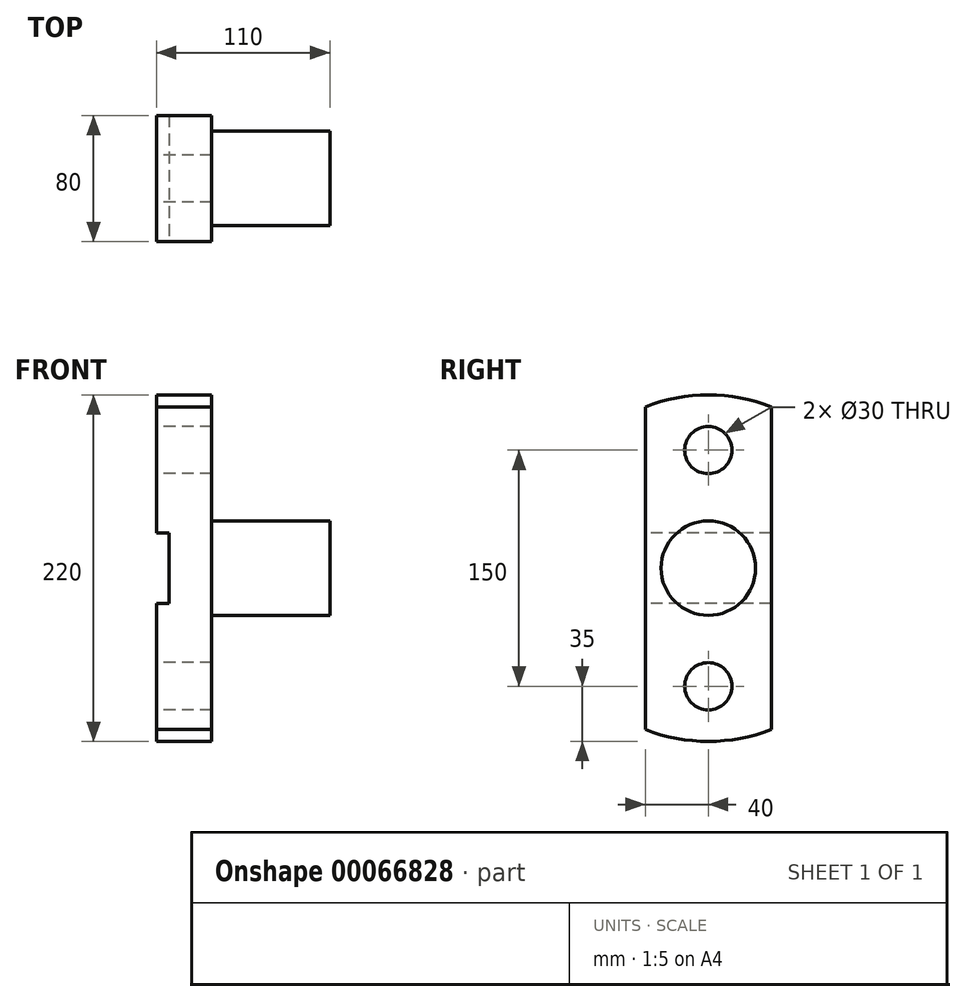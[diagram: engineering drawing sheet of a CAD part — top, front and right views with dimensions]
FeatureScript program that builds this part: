
annotation { "Feature Type Name" : "Feature", "Feature Type Description" : "" }
export const myFeature = defineFeature(function(context is Context, id is Id, definition is map)
    precondition{}
    {
        {
            var Q0;
            Q0=qCreatedBy(makeId("Right.planeOp"),FACE);
            var sketch = newSketch(context, id + "F0", { "sketchPlane" : qUnion([Q0])});
            skArc(sketch, "E0", {"start": v(-40, -102.47) * mm, "mid": v(0, -110) * mm, "end": v(40, -102.47) * mm});
            skLineSegment(sketch, "E1", {"start": v(-40, 102.47) * mm, "end": v(-40, -102.47) * mm});
            skLineSegment(sketch, "E2", {"start": v(40, 102.47) * mm, "end": v(40, -102.47) * mm});
            skArc(sketch, "E3.trimOffspring", {"start": v(40, 102.47) * mm, "mid": v(0, 110) * mm, "end": v(-40, 102.47) * mm});
            skCircle(sketch, "E4", {"center": v(0, 75) * mm, "radius": 15 * mm});
            skCircle(sketch, "E5", {"center": v(0, -75) * mm, "radius": 15 * mm});
            skSolve(sketch);
        }
        {
            var Q0;
            Q0=makeQuery(id+"F0.imprint","IMPRINT",FACE,{"disambiguationData":[TD([[makeQuery(id+"F0.imprint","IMPRINT",EDGE,{"derivedFrom":sQuery(id+"F0.wireOp",EDGE,"E0")}),1.0]])]});
            extrude(context, id + "F1", {"entities" : qUnion([Q0]), "depth" : 35 * mm});
        }
        {
            var Q0;
            Q0=makeQuery(id+"F1.opExtrude","CAP_FACE",FACE,{"disambiguationData":[OSD([sQuery(id+"F0.wireOp",EDGE,"E0"),sQuery(id+"F0.wireOp",EDGE,"E1"),sQuery(id+"F0.wireOp",EDGE,"E2"),sQuery(id+"F0.wireOp",EDGE,"E3.trimOffspring"),sQuery(id+"F0.wireOp",EDGE,"E4"),sQuery(id+"F0.wireOp",EDGE,"E5")])],"isStart":false});
            var sketch = newSketch(context, id + "F2", { "sketchPlane" : qUnion([Q0])});
            skCircle(sketch, "E6", {"center": v(0, 0) * mm, "radius": 30 * mm});
            skSolve(sketch);
        }
        {
            var Q0;
            Q0=makeQuery(id+"F2.imprint","IMPRINT",FACE,{"disambiguationData":[TD([[makeQuery(id+"F2.imprint","IMPRINT",EDGE,{"derivedFrom":sQuery(id+"F2.wireOp",EDGE,"E6")}),1.0]])]});
            extrude(context, id + "F3", {"entities" : qUnion([Q0]), "operationType" : NewBodyOperationType.ADD, "depth" : 75 * mm});
        }
        {
            var Q0;
            Q0=qCreatedBy(makeId("Front.planeOp"),FACE);
            var sketch = newSketch(context, id + "F4", { "sketchPlane" : qUnion([Q0])});
            skLineSegment(sketch, "E7.bottom", {"start": v(0, 22.5) * mm, "end": v(8, 22.5) * mm});
            skLineSegment(sketch, "E7.top", {"start": v(0, -22.5) * mm, "end": v(8, -22.5) * mm});
            skLineSegment(sketch, "E7.left", {"start": v(0, 22.5) * mm, "end": v(0, -22.5) * mm});
            skLineSegment(sketch, "E7.right", {"start": v(8, 22.5) * mm, "end": v(8, -22.5) * mm});
            skSolve(sketch);
        }
        {
            var Q0;
            Q0 = qSketchRegion(id + "F4", true);
            extrude(context, id + "F5", {"entities" : qUnion([Q0]), "operationType" : NewBodyOperationType.REMOVE, "endBound" : BoundingType.THROUGH_ALL, "oppositeDirection" : true, "depth" : 25 * mm, "hasSecondDirection" : true, "secondDirectionBound" : SecondDirectionBoundingType.THROUGH_ALL, "secondDirectionOppositeDirection" : false, "secondDirectionDepth" : 25 * mm});
        }
    });
